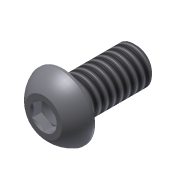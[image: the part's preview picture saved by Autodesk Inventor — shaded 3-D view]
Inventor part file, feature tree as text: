
AUTODESK INVENTOR PART (.ipt)
format: ipt  version: 2011 (Build 150239000, 239)  size: 205,824 bytes
history: native  units: in
note: dims shown in document units (in); Inventor stores cm internally (conversion verified against a paired STEP export)
features: extrude x2, sketch x2, other x1, imported_body x1, thread x1, chamfer x1
ambient origin geometry x8: Origin, YZ Plane, XZ Plane, XY Plane, X Axis, Y Axis, Z Axis, Center Point
feature tree (8):
  parser-record x1  (decoder bookkeeping rows leaked as tree rows — omitted from the tree; the rows remain in map.json)
  imported_body  "Base1"
  extrude  "Extrusion1"  Depth=1.0in TaperAngle=0.0deg
  extrude  "Extrusion2"  Depth=0.5in TaperAngle=0.0deg
  thread  "Thread1"  [1 undecoded]
  chamfer  "Chamfer1"  Distance=0.02in Angle=45.0deg
  sketch  "Sketch1"  dims[d1=0.26in d2=1.0in d3=0.0in]
  sketch  "Sketch2"  dims[d4=0.25in d5=0.5in d6=0.0in d7=1.0in d8=0.0in d9=0.02in d10=0.125in d11=45.0deg]
note: 1 required parameter value undecoded (feature->parameter linkage not recoverable at this tier; creation-order binding heuristic only, values carry confidence <= 0.55)
